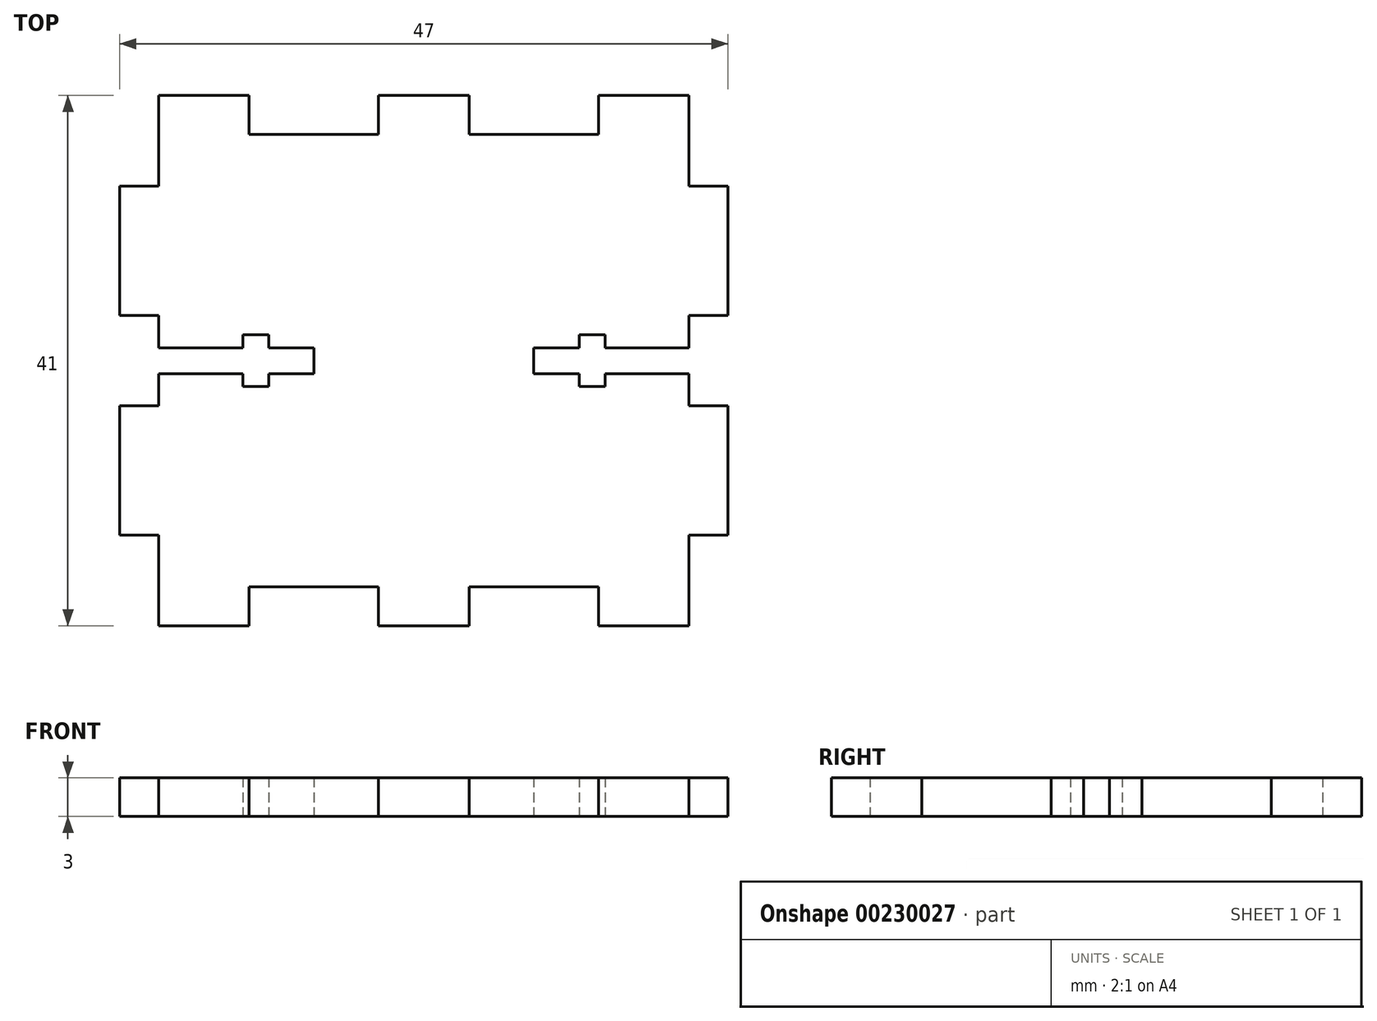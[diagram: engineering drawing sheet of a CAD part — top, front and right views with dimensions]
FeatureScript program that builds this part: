
annotation { "Feature Type Name" : "Feature", "Feature Type Description" : "" }
export const myFeature = defineFeature(function(context is Context, id is Id, definition is map)
    precondition{}
    {
        {
            var Q0;
            Q0=qCreatedBy(makeId("Top.planeOp"),FACE);
            var sketch = newSketch(context, id + "F0", { "sketchPlane" : qUnion([Q0])});
            skLineSegment(sketch, "E0", {"start": v(3.47, -20.5) * mm, "end": v(3.47, -17.5) * mm});
            skLineSegment(sketch, "E1", {"start": v(3.47, -17.5) * mm, "end": v(13.47, -17.5) * mm});
            skLineSegment(sketch, "E2", {"start": v(20.47, -13.5) * mm, "end": v(23.47, -13.5) * mm});
            skLineSegment(sketch, "E3", {"start": v(23.47, -13.5) * mm, "end": v(23.47, -3.5) * mm});
            skLineSegment(sketch, "E4", {"start": v(23.47, -3.5) * mm, "end": v(20.47, -3.5) * mm});
            skLineSegment(sketch, "E5", {"start": v(20.47, -3.5) * mm, "end": v(20.47, -1) * mm});
            skLineSegment(sketch, "E6", {"start": v(20.47, -1) * mm, "end": v(13.97, -1) * mm});
            skLineSegment(sketch, "E7", {"start": v(13.97, -1) * mm, "end": v(13.97, -2) * mm});
            skLineSegment(sketch, "E8", {"start": v(13.97, -2) * mm, "end": v(11.97, -2) * mm});
            skLineSegment(sketch, "E9", {"start": v(11.97, -2) * mm, "end": v(11.97, -1) * mm});
            skLineSegment(sketch, "E10", {"start": v(11.97, -1) * mm, "end": v(8.47, -1) * mm});
            skLineSegment(sketch, "E11", {"start": v(8.47, -1) * mm, "end": v(8.47, 0) * mm});
            skLineSegment(sketch, "E12", {"start": v(23.96, 0) * mm, "end": v(-20.53, 0) * mm, "construction": true});
            skLineSegment(sketch, "E13", {"start": v(-0.03, -20.5) * mm, "end": v(3.47, -20.5) * mm});
            skLineSegment(sketch, "E14", {"start": v(-0.03, 20.5) * mm, "end": v(-0.03, -20.5) * mm, "construction": true});
            skLineSegment(sketch, "E15", {"start": v(13.47, -17.5) * mm, "end": v(13.47, -20.5) * mm});
            skLineSegment(sketch, "E16", {"start": v(13.47, -20.5) * mm, "end": v(20.47, -20.5) * mm});
            skLineSegment(sketch, "E17", {"start": v(20.47, -20.5) * mm, "end": v(20.47, -13.5) * mm});
            skLineSegment(sketch, "E18.MirrorCS", {"start": v(13.97, 2) * mm, "end": v(11.97, 2) * mm});
            skLineSegment(sketch, "E19.MirrorCS", {"start": v(20.47, 13.5) * mm, "end": v(23.47, 13.5) * mm});
            skLineSegment(sketch, "E20.MirrorCS", {"start": v(8.47, 1) * mm, "end": v(8.47, 0) * mm});
            skLineSegment(sketch, "E21.MirrorCS", {"start": v(20.47, 3.5) * mm, "end": v(20.47, 1) * mm});
            skLineSegment(sketch, "E22.MirrorCS", {"start": v(11.97, 2) * mm, "end": v(11.97, 1) * mm});
            skLineSegment(sketch, "E23.MirrorCS", {"start": v(23.47, 3.5) * mm, "end": v(20.47, 3.5) * mm});
            skLineSegment(sketch, "E24.MirrorCS", {"start": v(13.97, 1) * mm, "end": v(13.97, 2) * mm});
            skLineSegment(sketch, "E25.MirrorCS", {"start": v(13.47, 20.5) * mm, "end": v(20.47, 20.5) * mm});
            skLineSegment(sketch, "E26.MirrorCS", {"start": v(20.47, 1) * mm, "end": v(13.97, 1) * mm});
            skLineSegment(sketch, "E27.MirrorCS", {"start": v(20.47, 20.5) * mm, "end": v(20.47, 13.5) * mm});
            skLineSegment(sketch, "E28.MirrorCS", {"start": v(11.97, 1) * mm, "end": v(8.47, 1) * mm});
            skLineSegment(sketch, "E29.MirrorCS", {"start": v(3.47, 20.5) * mm, "end": v(3.47, 17.5) * mm});
            skLineSegment(sketch, "E30.MirrorCS", {"start": v(3.47, 17.5) * mm, "end": v(13.47, 17.5) * mm});
            skLineSegment(sketch, "E31.MirrorCS", {"start": v(23.47, 13.5) * mm, "end": v(23.47, 3.5) * mm});
            skLineSegment(sketch, "E32.MirrorCS", {"start": v(-0.03, 20.5) * mm, "end": v(3.47, 20.5) * mm});
            skLineSegment(sketch, "E33.MirrorCS", {"start": v(13.47, 17.5) * mm, "end": v(13.47, 20.5) * mm});
            skLineSegment(sketch, "E34.MirrorCS", {"start": v(-8.53, 1) * mm, "end": v(-8.53, 0) * mm});
            skLineSegment(sketch, "E35.MirrorCS", {"start": v(-14.03, -1) * mm, "end": v(-14.03, -2) * mm});
            skLineSegment(sketch, "E36.MirrorCS", {"start": v(-8.53, -1) * mm, "end": v(-8.53, 0) * mm});
            skLineSegment(sketch, "E37.MirrorCS", {"start": v(-14.03, 2) * mm, "end": v(-12.03, 2) * mm});
            skLineSegment(sketch, "E38.MirrorCS", {"start": v(-14.03, 1) * mm, "end": v(-14.03, 2) * mm});
            skLineSegment(sketch, "E39.MirrorCS", {"start": v(-12.03, 1) * mm, "end": v(-8.53, 1) * mm});
            skLineSegment(sketch, "E40.MirrorCS", {"start": v(-12.03, -2) * mm, "end": v(-12.03, -1) * mm});
            skLineSegment(sketch, "E41.MirrorCS", {"start": v(-14.03, -2) * mm, "end": v(-12.03, -2) * mm});
            skLineSegment(sketch, "E42.MirrorCS", {"start": v(-12.03, -1) * mm, "end": v(-8.53, -1) * mm});
            skLineSegment(sketch, "E43.MirrorCS", {"start": v(-0.03, -20.5) * mm, "end": v(-3.53, -20.5) * mm});
            skLineSegment(sketch, "E44.MirrorCS", {"start": v(-13.53, -17.5) * mm, "end": v(-13.53, -20.5) * mm});
            skLineSegment(sketch, "E45.MirrorCS", {"start": v(-20.53, -13.5) * mm, "end": v(-23.53, -13.5) * mm});
            skLineSegment(sketch, "E46.MirrorCS", {"start": v(-20.53, -3.5) * mm, "end": v(-20.53, -1) * mm});
            skLineSegment(sketch, "E47.MirrorCS", {"start": v(-13.53, 17.5) * mm, "end": v(-13.53, 20.5) * mm});
            skLineSegment(sketch, "E48.MirrorCS", {"start": v(-12.03, 2) * mm, "end": v(-12.03, 1) * mm});
            skLineSegment(sketch, "E49.MirrorCS", {"start": v(-20.53, 13.5) * mm, "end": v(-23.53, 13.5) * mm});
            skLineSegment(sketch, "E50.MirrorCS", {"start": v(-3.53, -20.5) * mm, "end": v(-3.53, -17.5) * mm});
            skLineSegment(sketch, "E51.MirrorCS", {"start": v(-0.03, 20.5) * mm, "end": v(-3.53, 20.5) * mm});
            skLineSegment(sketch, "E52.MirrorCS", {"start": v(-3.53, 20.5) * mm, "end": v(-3.53, 17.5) * mm});
            skLineSegment(sketch, "E53.MirrorCS", {"start": v(-20.53, 3.5) * mm, "end": v(-20.53, 1) * mm});
            skLineSegment(sketch, "E54.MirrorCS", {"start": v(-23.53, 3.5) * mm, "end": v(-20.53, 3.5) * mm});
            skLineSegment(sketch, "E55.MirrorCS", {"start": v(-23.53, -3.5) * mm, "end": v(-20.53, -3.5) * mm});
            skLineSegment(sketch, "E56.MirrorCS", {"start": v(-23.53, 13.5) * mm, "end": v(-23.53, 3.5) * mm});
            skLineSegment(sketch, "E57.MirrorCS", {"start": v(-3.53, 17.5) * mm, "end": v(-13.53, 17.5) * mm});
            skLineSegment(sketch, "E58.MirrorCS", {"start": v(-13.53, 20.5) * mm, "end": v(-20.53, 20.5) * mm});
            skLineSegment(sketch, "E59.MirrorCS", {"start": v(-20.53, -1) * mm, "end": v(-14.03, -1) * mm});
            skLineSegment(sketch, "E60.MirrorCS", {"start": v(-20.53, 1) * mm, "end": v(-14.03, 1) * mm});
            skLineSegment(sketch, "E61.MirrorCS", {"start": v(-3.53, -17.5) * mm, "end": v(-13.53, -17.5) * mm});
            skLineSegment(sketch, "E62.MirrorCS", {"start": v(-20.53, -20.5) * mm, "end": v(-20.53, -13.5) * mm});
            skLineSegment(sketch, "E63.MirrorCS", {"start": v(-13.53, -20.5) * mm, "end": v(-20.53, -20.5) * mm});
            skLineSegment(sketch, "E64.MirrorCS", {"start": v(-20.53, 20.5) * mm, "end": v(-20.53, 13.5) * mm});
            skLineSegment(sketch, "E65.MirrorCS", {"start": v(-23.53, -13.5) * mm, "end": v(-23.53, -3.5) * mm});
            skSolve(sketch);
        }
        {
            var Q0;
            Q0 = qSketchRegion(id + "F0", true);
            extrude(context, id + "F1", {"entities" : qUnion([Q0]), "depth" : 3 * mm});
        }
    });
